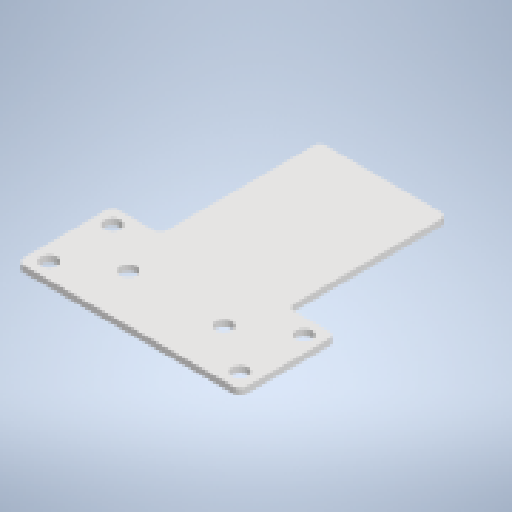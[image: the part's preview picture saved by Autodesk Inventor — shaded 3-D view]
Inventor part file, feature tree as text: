
AUTODESK INVENTOR PART (.ipt)
format: ipt  version: 2025 (Build 290162010, 162A)  size: 207,872 bytes
history: native  units: mm
features: other x2, sheet_metal_op x1, chamfer x1, sketch x1
ambient origin geometry x8: Origin, YZ Plane, XZ Plane, XY Plane, X Axis, Y Axis, Z Axis, Center Point
bodies: Solid1 (feature_tree)
feature tree (5):
  sheet_metal_op  "Face1"
  chamfer  "Corner Round1"
  sketch  "Sketch1"  dims[d0=40.0mm d1=50.0mm d2=2.0mm d33=70.0mm d34=5.0mm d35=30.0mm d36=30.0mm d37=2.0mm d38=5.0mm d39=5.0mm]
  other  "Plate1"
  other  "Definition1"
